# Revit family: HVAC_HangingSystems_Walraven_BIS_Strut_Rail_Beam_Clamp
name_source: partatom
category: Mechanical Equipment
revit_build: Autodesk Revit MEP 2016 (Build: 20150220_1215(x64)
units: mm (PartAtom-declared; Revit-internal decimal feet)

## family parameters
Cut with Voids When Loaded = No
Host = Face
OmniClass Number = 23.60.30.11.17
OmniClass Title = Pipework/Ductwork Mechanical Fasteners/Supports
Part Type = Normal
Room Calculation Point = No
Round Connector Dimension = Use Diameter
Shared = No

## types (2) — shared parameters
Assembly Code = 50
BIMobject category = Hanging Systems
BIMobject category code = hvac-hanging-systems
BIMobject main category = HVAC
BIMobject main category code = hvac
Brand url = https://www.walraven.com
Default Elevation = 1219 mm
Description = rail beam clamp
Design country = China
IFC Classification = Mechanical Fastener
IfcDescription = rail beam clamp
IfcExportAs = IfcMechanicalFastenerType
IfcExportType = USERDEFINED
Manufacturer = Walraven
Manufacturer country = China
Manufacturer name = Walraven
Material main = Steel
Model = BIS Strut Rail Beam Clamp
Nominal width = 80 mm  [stored 0.262467 ft]
OmniClass Code = 23-27 43 13
OmniClass Description = Mechanical Pipe Supports
Product Guid = c7702cfa-3de2-4be7-8ca3-7707251fd95f
Product SKU = bis-strut-rail-beam-clamp
Product data url = https://bimobject.com
Product family = Rail Systems
Product group = Beam Fixings
Product url = https://www.walraven.com
QR code = http://bimobject.com
RSen_C_code_ETIM = EC010150
RSen_C_code_ETIM_url = https://prod.etim-international.com
RSen_C_content_modification_date = 04-02-2019
RSen_C_content_releasedate = 22-01-2019
RSen_C_intended_use = hanging systems
RSen_C_level_of_development = LOD400
RSen_C_material = steel
RSen_C_material_colour = grey
RSen_C_material_finish = hot dip galvanized
RSen_S_max_allowed_load = 5700
Technical description = https://library.walraven.com
URL = https://www.walraven.com
Weight Net (Kg) = 0
gm_type1 = Strut Rail : 41x21
region_index = 1
zero-valued in all types: Edition number, Nominal height

## per-type parameters (varying)
| type | gm_type2 | gm_type3 | gm_type4 | gm_type5 | gm_type6 | gm_type7 | type_index |
| Strut 41x21+41x41+41x21D | Strut Rail : 41x21 | Strut Rail : 41x21 | Strut Rail : 41x21 | Strut Rail : 41x21 | Strut Rail : 41x21 | Strut Rail : 41x21 | 1 |
| Strut 41x62+41x82+41x41D+DS 5 (41x51) | Strut Rail : 41x41 | Strut Rail : 41x21D | Strut Rail : 41x62 | Strut Rail : 41x82 | Strut Rail : 41x41D | Strut Rail : DS 5 (41x51) | 2 |

note: [stored X ft] marks values corroborated as IEEE doubles in the binary element streams (Revit-internal decimal feet)

## geometry (parser evidence)
native form markers: Blend x2, Sweep x6
no freeform markers — native parametric forms only
